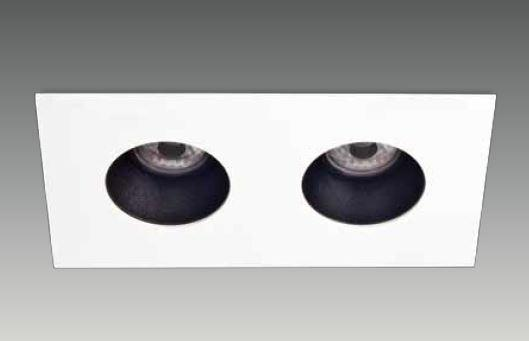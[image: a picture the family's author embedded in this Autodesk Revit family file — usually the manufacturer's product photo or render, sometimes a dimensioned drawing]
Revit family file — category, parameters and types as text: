
# Revit family: DG 2213 SAY
name_source: partatom
category: Lighting Fixtures
revit_build: Autodesk Revit 2017 (Build: 20160225_1515(x64)
units: mm (PartAtom-declared; Revit-internal decimal feet)

## family parameters
Always vertical = Yes
Cut with Voids When Loaded = No
Host = Ceiling
Light Source = Yes
OmniClass Number = 23.80.70.11
OmniClass Title = Luminaries for Internal Lighting
Part Type = Normal
Room Calculation Point = No
Round Connector Dimension = Use Diameter
Shared = No

## types (2) — shared parameters
Apparent Load = 15 VA
Color Filter = 16777215
Dimming Lamp Color Temperature Shift = <None>
Emit Shape Visible in Rendering = Yes
Emit from Circle Diameter = 70 mm  [stored 0.229659 ft]
Light Source Symbol Length = 3048 mm  [stored 10 ft]
Manufacturer = ARLIGHT
Spot Beam Angle = 35.00°
Spot Field Angle = 90.00°
Tilt Angle = 90.00°
Type Image = DG 2213 SAY.JPG
Wattage Comments = 15W

## type names (no varying parameters)
- DGSAY.2213.15.30.35
- DGSAY.2213.15.40.35

note: [stored X ft] marks values corroborated as IEEE doubles in the binary element streams (Revit-internal decimal feet)

## geometry (parser evidence)
native form markers: Sweep x4
no freeform markers — native parametric forms only
